# Revit family: CENTUM Gelenkverbindung XL120
name_source: partatom
category: HLS-Bauteile
revit_build: Autodesk Revit 2017 (Build: 20190508_0315(x64)
units: mm (PartAtom-declared; Revit-internal decimal feet)

## family parameters
Arbeitsebenenbasiert = Ja
Beim Laden mit Abzugskörper schneiden = Nein
Bemaßung runder Anschluss = Durchmesser verwenden
Gemeinsam genutzt = Ja
Immer vertikal = Nein
Raumberechnungspunkt = Nein
Teiletyp = Normal

## types (1)
- CENTUM Gelenkverbindung XL120
    Artikelnummer = 1641214110
    Ausrichtung = längs
    EAN = 4250928437129
    Fabrikat = MEFA
    Firma = MEFA Befestigungs- und Montagesysteme GmbH
    Gewicht = 1.31 kg
    Gewicht pro Bauteil = 1.31 kg
    Kurztext1 = Gelenkverbindung CENTUM XL 120
    Kurztext2 = C-Profil längs max. Winkel 90 ° ZnNi
    Lochdurchmesser = 13 mm
    Material = Stahl
    Mengeneinheit = St
    Oberflaeche = Zink-Nickel
    Profil = CENTUM
    Profiltyp = XL 120
    Vorgabe-Ansicht = 1219 mm
    Winkel = 90 °
    max. zul. Last = 7.00 kN
    vpe = 1 St

## geometry (parser evidence)
native form markers: Sweep x2
no freeform markers — native parametric forms only
